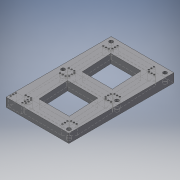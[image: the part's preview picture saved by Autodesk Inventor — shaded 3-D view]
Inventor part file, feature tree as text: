
AUTODESK INVENTOR PART (.ipt)
format: ipt  version: 2016 SP2 (Build 200236200, 236)  size: 750,592 bytes
history: native  units: mm
features: reference x21, extrude x12, sketch x12, projected_geometry x5, chamfer x1
ambient origin geometry x8: Origin, YZ Plane, XZ Plane, XY Plane, X Axis, Y Axis, Z Axis, Center Point
bodies: Volumenkörper1 (feature_tree)
feature tree (51):
  extrude  "Extrusion1"  Depth=0.2mm
  extrude  "Extrusion2"  Depth=0.2mm
  extrude  "Extrusion3"  Depth=0.2mm
  extrude  "Extrusion4"  Depth=0.2mm
  extrude  "Extrusion5"  Depth=0.2mm
  extrude  "Extrusion6"  Depth=0.2mm
  chamfer  "Fase1"  Distance=10.4mm
  extrude  "Extrusion7"  Depth=10.4mm
  extrude  "Extrusion8"  Depth=50.4mm
  extrude  "Extrusion9"  Depth=0.2mm
  extrude  "Extrusion10"  Depth=0.2mm
  extrude  "Extrusion11"  Depth=0.2mm
  extrude  "Extrusion12"  TaperAngle=90.0deg  [1 undecoded]
  sketch  "Skizze1"  dims[d0=0.2mm d1=0.2mm]
  reference  "Referenz1"
  reference  "Referenz2"
  reference  "Referenz3"
  reference  "Referenz4"
  reference  "Referenz5"
  reference  "Referenz6"
  reference  "Referenz7"
  reference  "Referenz8"
  reference  "Referenz9"
  reference  "Referenz10"
  reference  "Referenz11"
  reference  "Referenz12"
  reference  "Referenz13"
  reference  "Referenz14"
  sketch  "Skizze2"  dims[d2=0.2mm d3=0.2mm]
  reference  "Referenz15"
  reference  "Referenz16"
  projected_geometry  "Projizierte Kontur1"
  sketch  "Skizze3"  dims[d4=0.2mm d5=0.2mm]
  reference  "Referenz17"
  sketch  "Skizze4"  dims[d6=0.2mm d7=0.2mm]
  sketch  "Skizze5"  dims[d8=0.2mm d9=0.2mm]
  projected_geometry  "Projizierte Kontur2"
  projected_geometry  "Projizierte Kontur3"
  sketch  "Skizze6"  dims[d10=0.2mm d11=0.2mm]
  projected_geometry  "Projizierte Kontur4"
  projected_geometry  "Projizierte Kontur5"
  sketch  "Skizze7"  dims[d12=0.2mm]
  sketch  "Skizze8"  dims[d13=0.2mm]
  sketch  "Skizze9"  dims[d14=0.2mm d16=10.4mm d17=10.4mm]
  reference  "Referenz18"
  reference  "Referenz19"
  reference  "Referenz20"
  reference  "Referenz21"
  sketch  "Skizze10"  dims[d18=10.4mm d19=10.4mm]
  sketch  "Skizze12"  dims[d20=50.4mm d21=50.4mm d22=50.4mm]
  sketch  "Skizze13"  dims[d23=50.4mm d24=0.2mm d25=0.2mm d26=0.2mm d28=90.0deg d29=50.4mm d30=0.2mm d31=0.2mm d32=10.4mm d33=11.0mm d34=0.0mm d35=17.0mm d36=11.0mm d37=5.5mm d38=1.2mm d39=0.282455mm d40=0.282455mm d41=0.282455mm d42=0.282455mm d43=0.282455mm d44=0.282455mm d45=0.282455mm d46=9.0mm d47=0.0mm d49=5.0mm d50=5.0mm d51=5.0mm d52=5.0mm d54=5.0mm d56=5.0mm d57=5.0mm d58=5.0mm d59=11.0mm d60=5.5mm d61=1.2mm d62=17.0mm d63=1.2mm d64=11.0mm d65=0.0mm d66=11.0mm d67=17.0mm d68=4.0mm d69=0.0mm d70=2.0mm d71=0.0mm d72=1.5mm d73=0.0mm d74=1.5mm d75=2.0mm d76=45.0deg d77=1.0mm d78=0.0mm d79=0.5mm d80=0.5mm d81=0.5mm d82=0.5mm d83=0.5mm d84=0.5mm d85=0.5mm d86=0.5mm d87=0.5mm d88=0.5mm d89=0.5mm d90=0.5mm d91=0.5mm d92=0.5mm d93=0.5mm d94=0.5mm d95=2.0mm d96=2.0mm d97=2.0mm d98=2.0mm d99=2.0mm d100=2.0mm d101=2.0mm d102=2.0mm d103=2.0mm d104=2.0mm d105=2.0mm d106=2.0mm d107=2.0mm d108=2.0mm d109=2.0mm d110=2.0mm d111=2.0mm d112=2.0mm d113=2.0mm d114=2.0mm d115=2.0mm d116=2.0mm d117=2.0mm d118=2.0mm d119=2.0mm d120=2.0mm d121=2.0mm d122=2.0mm d123=2.0mm d124=2.0mm d125=2.0mm d126=2.0mm d127=2.0mm d128=2.0mm d129=2.0mm d130=2.0mm d131=2.0mm d132=2.0mm d133=2.0mm d134=2.0mm d135=2.0mm d136=2.0mm d137=2.0mm d138=2.0mm d139=2.0mm d140=2.0mm d141=2.0mm d142=2.0mm d143=3.5mm d144=3.5mm d145=3.5mm d146=3.5mm d147=3.5mm d148=3.5mm d149=3.5mm d150=3.5mm d151=3.5mm d152=3.5mm d153=3.5mm d154=3.5mm d155=3.5mm d156=3.5mm d157=3.5mm d158=3.5mm d159=3.5mm d160=3.5mm d161=3.5mm d162=3.5mm d163=3.5mm d164=3.5mm d165=3.5mm d166=3.5mm d167=3.5mm d168=3.5mm d169=3.5mm d170=3.5mm d171=3.5mm d172=3.5mm d173=3.5mm d174=3.5mm d175=1.0mm d176=0.0mm d177=5.0mm d178=5.0mm d179=5.0mm d180=5.0mm d181=5.0mm d182=6.0mm d183=6.0mm d184=6.0mm d185=6.0mm d186=6.0mm d187=6.0mm d188=71.34569mm d189=71.34569mm d190=5.0mm d191=5.0mm d192=3.0mm d193=0.0mm d194=3.0mm d195=0.0mm d197=0.2mm d198=0.2mm d199=0.2mm d200=0.2mm d201=0.2mm d202=0.2mm d203=0.2mm d204=0.2mm d205=0.2mm d206=0.2mm d207=0.2mm d208=0.2mm d209=0.2mm d210=0.2mm d211=9.0mm d212=0.0mm d213=0.2mm d214=0.2mm d215=7.0mm d216=0.0mm]
note: 1 required parameter value undecoded (feature->parameter linkage not recoverable at this tier; creation-order binding heuristic only, values carry confidence <= 0.55)
